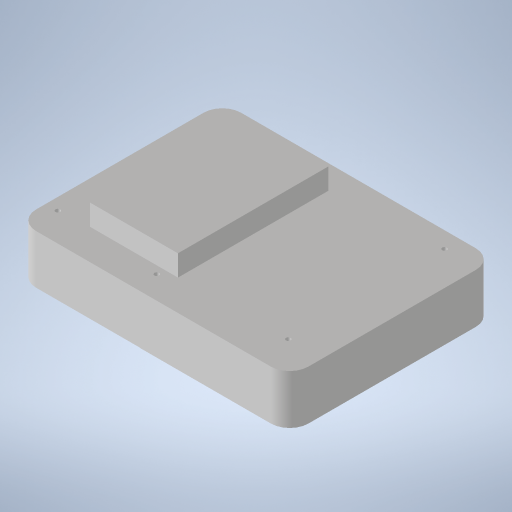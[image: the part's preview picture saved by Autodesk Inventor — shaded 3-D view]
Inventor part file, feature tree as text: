
AUTODESK INVENTOR PART (.ipt)
format: ipt  version: 2023.1 (Build 271208000, 208)  size: 313,344 bytes
history: native  units: mm
features: sketch x5, projected_geometry x5, extrude x4, hole x1
ambient origin geometry x8: Origin, YZ Plane, XZ Plane, XY Plane, X Axis, Y Axis, Z Axis, Center Point
bodies: Volumenkörper1 (feature_tree)
feature tree (15):
  extrude  "Extrusion1"  Depth=87.7mm
  extrude  "Extrusion2"  Depth=21.0mm TaperAngle=0.0deg
  extrude  "Extrusion3"  Depth=0.1mm TaperAngle=0.0deg
  hole  "Bohrung1"  [1 undecoded]
  extrude  "Extrusion4"  Depth=10.3mm
  sketch  "Skizze1"  dims[d0=116.5mm d1=87.7mm]
  sketch  "Skizze2"  dims[d2=8.0mm d3=21.0mm d4=0.0mm]
  projected_geometry  "Projizierte Kontur1"
  sketch  "Skizze3"  dims[d5=64.0mm d6=0.1mm d7=0.0mm]
  sketch  "Skizze4"  dims[d8=37.6mm d9=64.3mm]
  projected_geometry  "Projizierte Kontur2"
  projected_geometry  "Projizierte Kontur3"
  sketch  "Skizze5"  dims[d10=13.1mm d11=10.3mm d12=18.0mm d13=9.0mm d14=0.0mm d15=2.2mm d16=2.2mm d17=2.2mm d18=2.2mm d19=2.2mm d20=2.2mm d21=0.0mm d22=66.85mm d23=70.0mm d24=66.5mm d25=52.2mm d26=44.7mm d27=36.0mm d28=55.7mm d29=118.7mm d30=112.280925mm d31=86.3mm d32=88.069121mm d33=79.397605mm d34=13.9mm d35=6.95mm d36=14.5mm d37=9.818131mm d38=7.881869mm d39=9.007129mm d40=12.192871mm d41=5.1mm d42=2.0mm d43=6.0mm d44=10.5mm d45=22.0mm d46=14.3117mm d47=8.0mm d48=20.594885mm d49=9.0mm d50=3.3mm d51=1.0mm d52=15.05mm d53=14.13mm d54=6.0mm d55=0.0mm]
  projected_geometry  "Projizierte Kontur4"
  projected_geometry  "Projizierte Kontur5"
note: 1 required parameter value undecoded (feature->parameter linkage not recoverable at this tier; creation-order binding heuristic only, values carry confidence <= 0.55)
